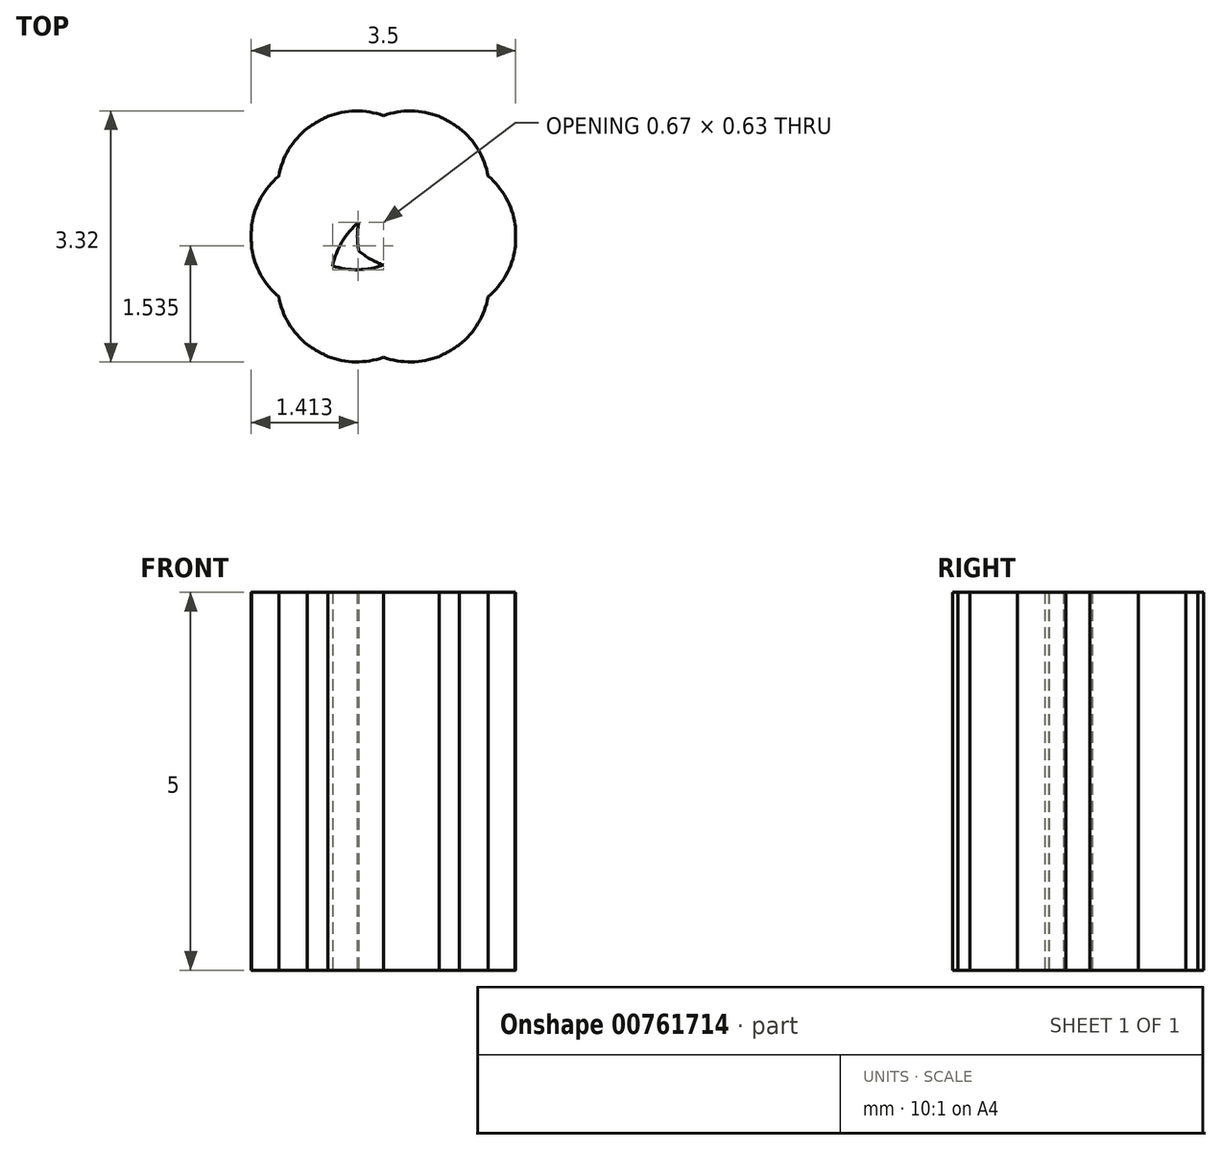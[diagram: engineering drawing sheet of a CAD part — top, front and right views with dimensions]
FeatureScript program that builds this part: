
annotation { "Feature Type Name" : "Feature", "Feature Type Description" : "" }
export const myFeature = defineFeature(function(context is Context, id is Id, definition is map)
    precondition{}
    {
        {
            var Q0;
            Q0=qCreatedBy(makeId("Top.planeOp"),FACE);
            var sketch = newSketch(context, id + "F0", { "sketchPlane" : qUnion([Q0])});
            skCircle(sketch, "E0", {"center": v(0, 0) * mm, "radius": 1.75 * mm});
            skCircle(sketch, "E1", {"center": v(-0.7, 0) * mm, "radius": 1.05 * mm});
            skCircle(sketch, "E2.1.0", {"center": v(-0.35, -0.61) * mm, "radius": 1.05 * mm});
            skCircle(sketch, "E2.2.0", {"center": v(0.35, -0.61) * mm, "radius": 1.05 * mm});
            skCircle(sketch, "E2.3.0", {"center": v(0.7, 0) * mm, "radius": 1.05 * mm});
            skCircle(sketch, "E2.4.0", {"center": v(0.35, 0.61) * mm, "radius": 1.05 * mm});
            skCircle(sketch, "E2.5.0", {"center": v(-0.35, 0.61) * mm, "radius": 1.05 * mm});
            skSolve(sketch);
        }
        {
            var Q0;
            {var subQ0=sQuery(id+"F0.wireOp",EDGE,"E2.5.0");var subQ1=sQuery(id+"F0.wireOp",EDGE,"E0");var subQ2=makeQuery(id+"F0.imprint","INTERSECT",VERTEX,{"disambiguationData":[OD(0.0)],"derivedFrom":[subQ1,subQ0]});Q0=makeQuery(id+"F0.imprint","IMPRINT",FACE,{"disambiguationData":[TD([[makeQuery(id+"F0.imprint","IMPRINT",EDGE,{"disambiguationData":[TD([[subQ2,-1.0]])],"derivedFrom":subQ1}),1.0]])]});}
            var Q1;
            {var subQ0=sQuery(id+"F0.wireOp",EDGE,"E2.4.0");var subQ1=sQuery(id+"F0.wireOp",EDGE,"E1");var subQ2=makeQuery(id+"F0.imprint","INTERSECT",VERTEX,{"disambiguationData":[OD(0.0)],"derivedFrom":[subQ1,subQ0]});Q1=makeQuery(id+"F0.imprint","IMPRINT",FACE,{"disambiguationData":[TD([[makeQuery(id+"F0.imprint","IMPRINT",EDGE,{"disambiguationData":[TD([[subQ2,-1.0]])],"derivedFrom":subQ1}),1.0]])]});}
            var Q2;
            {var subQ0=sQuery(id+"F0.wireOp",EDGE,"E2.3.0");var subQ1=sQuery(id+"F0.wireOp",EDGE,"E1");var subQ2=makeQuery(id+"F0.imprint","INTERSECT",VERTEX,{"disambiguationData":[OD(0.0)],"derivedFrom":[subQ1,subQ0]});Q2=makeQuery(id+"F0.imprint","IMPRINT",FACE,{"disambiguationData":[TD([[makeQuery(id+"F0.imprint","IMPRINT",EDGE,{"disambiguationData":[TD([[subQ2,-1.0]])],"derivedFrom":subQ1}),-1.0]])]});}
            var Q3;
            {var subQ0=sQuery(id+"F0.wireOp",EDGE,"E2.4.0");var subQ1=sQuery(id+"F0.wireOp",EDGE,"E0");var subQ2=makeQuery(id+"F0.imprint","INTERSECT",VERTEX,{"disambiguationData":[OD(0.0)],"derivedFrom":[subQ1,subQ0]});Q3=makeQuery(id+"F0.imprint","IMPRINT",FACE,{"disambiguationData":[TD([[makeQuery(id+"F0.imprint","IMPRINT",EDGE,{"disambiguationData":[TD([[subQ2,-1.0]])],"derivedFrom":subQ1}),1.0]])]});}
            var Q4;
            {var subQ0=sQuery(id+"F0.wireOp",EDGE,"E2.4.0");var subQ1=sQuery(id+"F0.wireOp",EDGE,"E2.2.0");var subQ2=makeQuery(id+"F0.imprint","INTERSECT",VERTEX,{"disambiguationData":[OD(1.0)],"derivedFrom":[subQ1,subQ0]});Q4=makeQuery(id+"F0.imprint","IMPRINT",FACE,{"disambiguationData":[TD([[makeQuery(id+"F0.imprint","IMPRINT",EDGE,{"disambiguationData":[TD([[subQ2,-1.0]])],"derivedFrom":subQ1}),-1.0]])]});}
            var Q5;
            {var subQ0=sQuery(id+"F0.wireOp",EDGE,"E2.3.0");var subQ1=sQuery(id+"F0.wireOp",EDGE,"E0");var subQ2=makeQuery(id+"F0.imprint","INTERSECT",VERTEX,{"disambiguationData":[OD(0.0)],"derivedFrom":[subQ1,subQ0]});Q5=makeQuery(id+"F0.imprint","IMPRINT",FACE,{"disambiguationData":[TD([[makeQuery(id+"F0.imprint","IMPRINT",EDGE,{"disambiguationData":[TD([[subQ2,1.0]])],"derivedFrom":subQ1}),1.0]])]});}
            var Q6;
            {var subQ0=sQuery(id+"F0.wireOp",EDGE,"E2.3.0");var subQ1=sQuery(id+"F0.wireOp",EDGE,"E2.1.0");var subQ2=makeQuery(id+"F0.imprint","INTERSECT",VERTEX,{"disambiguationData":[OD(1.0)],"derivedFrom":[subQ1,subQ0]});Q6=makeQuery(id+"F0.imprint","IMPRINT",FACE,{"disambiguationData":[TD([[makeQuery(id+"F0.imprint","IMPRINT",EDGE,{"disambiguationData":[TD([[subQ2,-1.0]])],"derivedFrom":subQ1}),-1.0]])]});}
            var Q7;
            {var subQ0=sQuery(id+"F0.wireOp",EDGE,"E2.2.0");var subQ1=sQuery(id+"F0.wireOp",EDGE,"E0");var subQ8=makeQuery(id+"F0.imprint","INTERSECT",VERTEX,{"disambiguationData":[OD(0.0)],"derivedFrom":[subQ1,subQ0]});Q7=makeQuery(id+"F0.imprint","IMPRINT",FACE,{"disambiguationData":[TD([[makeQuery(id+"F0.imprint","IMPRINT",EDGE,{"disambiguationData":[TD([[subQ8,-1.0]])],"derivedFrom":subQ1}),1.0]])]});}
            var Q8;
            {var subQ0=sQuery(id+"F0.wireOp",EDGE,"E2.2.0");var subQ1=sQuery(id+"F0.wireOp",EDGE,"E1");var subQ2=makeQuery(id+"F0.imprint","INTERSECT",VERTEX,{"disambiguationData":[OD(1.0)],"derivedFrom":[subQ1,subQ0]});Q8=makeQuery(id+"F0.imprint","IMPRINT",FACE,{"disambiguationData":[TD([[makeQuery(id+"F0.imprint","IMPRINT",EDGE,{"disambiguationData":[TD([[subQ2,-1.0]])],"derivedFrom":subQ1}),-1.0]])]});}
            var Q9;
            {var subQ0=sQuery(id+"F0.wireOp",EDGE,"E2.1.0");var subQ1=sQuery(id+"F0.wireOp",EDGE,"E0");var subQ8=makeQuery(id+"F0.imprint","INTERSECT",VERTEX,{"disambiguationData":[OD(0.0)],"derivedFrom":[subQ1,subQ0]});Q9=makeQuery(id+"F0.imprint","IMPRINT",FACE,{"disambiguationData":[TD([[makeQuery(id+"F0.imprint","IMPRINT",EDGE,{"disambiguationData":[TD([[subQ8,-1.0]])],"derivedFrom":subQ1}),1.0]])]});}
            var Q10;
            {var subQ1=sQuery(id+"F0.wireOp",EDGE,"E1");var subQ5=sQuery(id+"F0.wireOp",EDGE,"E0");var subQ6=makeQuery(id+"F0.imprint","INTERSECT",VERTEX,{"disambiguationData":[OD(0.0)],"derivedFrom":[subQ5,subQ1]});Q10=makeQuery(id+"F0.imprint","IMPRINT",FACE,{"disambiguationData":[TD([[makeQuery(id+"F0.imprint","IMPRINT",EDGE,{"disambiguationData":[TD([[subQ6,-1.0]])],"derivedFrom":subQ5}),1.0]])]});}
            var Q11;
            {var subQ0=sQuery(id+"F0.wireOp",EDGE,"E2.1.0");var subQ1=sQuery(id+"F0.wireOp",EDGE,"E1");var subQ2=makeQuery(id+"F0.imprint","INTERSECT",VERTEX,{"disambiguationData":[OD(1.0)],"derivedFrom":[subQ1,subQ0]});Q11=makeQuery(id+"F0.imprint","IMPRINT",FACE,{"disambiguationData":[TD([[makeQuery(id+"F0.imprint","IMPRINT",EDGE,{"disambiguationData":[TD([[subQ2,-1.0]])],"derivedFrom":subQ1}),1.0]])]});}
            var Q12;
            {var subQ0=sQuery(id+"F0.wireOp",EDGE,"E2.2.0");var subQ1=sQuery(id+"F0.wireOp",EDGE,"E1");var subQ2=makeQuery(id+"F0.imprint","INTERSECT",VERTEX,{"disambiguationData":[OD(1.0)],"derivedFrom":[subQ1,subQ0]});Q12=makeQuery(id+"F0.imprint","IMPRINT",FACE,{"disambiguationData":[TD([[makeQuery(id+"F0.imprint","IMPRINT",EDGE,{"disambiguationData":[TD([[subQ2,-1.0]])],"derivedFrom":subQ1}),1.0]])]});}
            var Q13;
            {var subQ0=sQuery(id+"F0.wireOp",EDGE,"E2.3.0");var subQ1=sQuery(id+"F0.wireOp",EDGE,"E1");var subQ2=makeQuery(id+"F0.imprint","INTERSECT",VERTEX,{"disambiguationData":[OD(1.0)],"derivedFrom":[subQ1,subQ0]});Q13=makeQuery(id+"F0.imprint","IMPRINT",FACE,{"disambiguationData":[TD([[makeQuery(id+"F0.imprint","IMPRINT",EDGE,{"disambiguationData":[TD([[subQ2,-1.0]])],"derivedFrom":subQ1}),-1.0]])]});}
            var Q14;
            {var subQ0=sQuery(id+"F0.wireOp",EDGE,"E2.3.0");var subQ1=sQuery(id+"F0.wireOp",EDGE,"E1");var subQ2=makeQuery(id+"F0.imprint","INTERSECT",VERTEX,{"disambiguationData":[OD(1.0)],"derivedFrom":[subQ1,subQ0]});Q14=makeQuery(id+"F0.imprint","IMPRINT",FACE,{"disambiguationData":[TD([[makeQuery(id+"F0.imprint","IMPRINT",EDGE,{"disambiguationData":[TD([[subQ2,-1.0]])],"derivedFrom":subQ1}),1.0]])]});}
            var Q15;
            {var subQ0=sQuery(id+"F0.wireOp",EDGE,"E2.4.0");var subQ1=sQuery(id+"F0.wireOp",EDGE,"E2.1.0");var subQ2=makeQuery(id+"F0.imprint","INTERSECT",VERTEX,{"disambiguationData":[OD(1.0)],"derivedFrom":[subQ1,subQ0]});Q15=makeQuery(id+"F0.imprint","IMPRINT",FACE,{"disambiguationData":[TD([[makeQuery(id+"F0.imprint","IMPRINT",EDGE,{"disambiguationData":[TD([[subQ2,-1.0]])],"derivedFrom":subQ1}),-1.0]])]});}
            var Q16;
            {var subQ0=sQuery(id+"F0.wireOp",EDGE,"E2.2.0");var subQ1=sQuery(id+"F0.wireOp",EDGE,"E1");var subQ2=makeQuery(id+"F0.imprint","INTERSECT",VERTEX,{"disambiguationData":[OD(0.0)],"derivedFrom":[subQ1,subQ0]});Q16=makeQuery(id+"F0.imprint","IMPRINT",FACE,{"disambiguationData":[TD([[makeQuery(id+"F0.imprint","IMPRINT",EDGE,{"disambiguationData":[TD([[subQ2,-1.0]])],"derivedFrom":subQ1}),-1.0]])]});}
            var Q17;
            {var subQ0=sQuery(id+"F0.wireOp",EDGE,"E2.3.0");var subQ1=sQuery(id+"F0.wireOp",EDGE,"E1");var subQ2=makeQuery(id+"F0.imprint","INTERSECT",VERTEX,{"disambiguationData":[OD(0.0)],"derivedFrom":[subQ1,subQ0]});Q17=makeQuery(id+"F0.imprint","IMPRINT",FACE,{"disambiguationData":[TD([[makeQuery(id+"F0.imprint","IMPRINT",EDGE,{"disambiguationData":[TD([[subQ2,-1.0]])],"derivedFrom":subQ1}),1.0]])]});}
            var Q18;
            {var subQ0=sQuery(id+"F0.wireOp",EDGE,"E2.4.0");var subQ1=sQuery(id+"F0.wireOp",EDGE,"E2.1.0");var subQ2=makeQuery(id+"F0.imprint","INTERSECT",VERTEX,{"disambiguationData":[OD(0.0)],"derivedFrom":[subQ1,subQ0]});Q18=makeQuery(id+"F0.imprint","IMPRINT",FACE,{"disambiguationData":[TD([[makeQuery(id+"F0.imprint","IMPRINT",EDGE,{"disambiguationData":[TD([[subQ2,-1.0]])],"derivedFrom":subQ1}),1.0]])]});}
            var Q19;
            {var subQ0=sQuery(id+"F0.wireOp",EDGE,"E2.2.0");var subQ1=sQuery(id+"F0.wireOp",EDGE,"E1");var subQ2=makeQuery(id+"F0.imprint","INTERSECT",VERTEX,{"disambiguationData":[OD(0.0)],"derivedFrom":[subQ1,subQ0]});Q19=makeQuery(id+"F0.imprint","IMPRINT",FACE,{"disambiguationData":[TD([[makeQuery(id+"F0.imprint","IMPRINT",EDGE,{"disambiguationData":[TD([[subQ2,-1.0]])],"derivedFrom":subQ1}),1.0]])]});}
            var Q20;
            {var subQ0=sQuery(id+"F0.wireOp",EDGE,"E2.4.0");var subQ1=sQuery(id+"F0.wireOp",EDGE,"E1");var subQ2=makeQuery(id+"F0.imprint","INTERSECT",VERTEX,{"disambiguationData":[OD(1.0)],"derivedFrom":[subQ1,subQ0]});Q20=makeQuery(id+"F0.imprint","IMPRINT",FACE,{"disambiguationData":[TD([[makeQuery(id+"F0.imprint","IMPRINT",EDGE,{"disambiguationData":[TD([[subQ2,-1.0]])],"derivedFrom":subQ1}),-1.0]])]});}
            var Q21;
            {var subQ0=sQuery(id+"F0.wireOp",EDGE,"E2.4.0");var subQ1=sQuery(id+"F0.wireOp",EDGE,"E2.2.0");var subQ2=makeQuery(id+"F0.imprint","INTERSECT",VERTEX,{"disambiguationData":[OD(0.0)],"derivedFrom":[subQ1,subQ0]});Q21=makeQuery(id+"F0.imprint","IMPRINT",FACE,{"disambiguationData":[TD([[makeQuery(id+"F0.imprint","IMPRINT",EDGE,{"disambiguationData":[TD([[subQ2,-1.0]])],"derivedFrom":subQ1}),1.0]])]});}
            var Q22;
            {var subQ0=sQuery(id+"F0.wireOp",EDGE,"E2.3.0");var subQ1=sQuery(id+"F0.wireOp",EDGE,"E2.1.0");var subQ2=makeQuery(id+"F0.imprint","INTERSECT",VERTEX,{"disambiguationData":[OD(0.0)],"derivedFrom":[subQ1,subQ0]});Q22=makeQuery(id+"F0.imprint","IMPRINT",FACE,{"disambiguationData":[TD([[makeQuery(id+"F0.imprint","IMPRINT",EDGE,{"disambiguationData":[TD([[subQ2,-1.0]])],"derivedFrom":subQ1}),1.0]])]});}
            var Q23;
            {var subQ0=sQuery(id+"F0.wireOp",EDGE,"E2.2.0");var subQ1=sQuery(id+"F0.wireOp",EDGE,"E1");var subQ2=makeQuery(id+"F0.imprint","INTERSECT",VERTEX,{"disambiguationData":[OD(0.0)],"derivedFrom":[subQ1,subQ0]});Q23=makeQuery(id+"F0.imprint","IMPRINT",FACE,{"disambiguationData":[TD([[makeQuery(id+"F0.imprint","IMPRINT",EDGE,{"disambiguationData":[TD([[subQ2,1.0]])],"derivedFrom":subQ1}),-1.0]])]});}
            var Q24;
            {var subQ0=sQuery(id+"F0.wireOp",EDGE,"E2.4.0");var subQ1=sQuery(id+"F0.wireOp",EDGE,"E2.2.0");var subQ2=makeQuery(id+"F0.imprint","INTERSECT",VERTEX,{"disambiguationData":[OD(0.0)],"derivedFrom":[subQ1,subQ0]});Q24=makeQuery(id+"F0.imprint","IMPRINT",FACE,{"disambiguationData":[TD([[makeQuery(id+"F0.imprint","IMPRINT",EDGE,{"disambiguationData":[TD([[subQ2,1.0]])],"derivedFrom":subQ1}),1.0]])]});}
            var Q25;
            {var subQ0=sQuery(id+"F0.wireOp",EDGE,"E2.5.0");var subQ1=sQuery(id+"F0.wireOp",EDGE,"E2.3.0");var subQ2=makeQuery(id+"F0.imprint","INTERSECT",VERTEX,{"disambiguationData":[OD(0.0)],"derivedFrom":[subQ1,subQ0]});Q25=makeQuery(id+"F0.imprint","IMPRINT",FACE,{"disambiguationData":[TD([[makeQuery(id+"F0.imprint","IMPRINT",EDGE,{"disambiguationData":[TD([[subQ2,1.0]])],"derivedFrom":subQ1}),1.0]])]});}
            var Q26;
            {var subQ0=sQuery(id+"F0.wireOp",EDGE,"E2.4.0");var subQ1=sQuery(id+"F0.wireOp",EDGE,"E1");var subQ2=makeQuery(id+"F0.imprint","INTERSECT",VERTEX,{"disambiguationData":[OD(1.0)],"derivedFrom":[subQ1,subQ0]});Q26=makeQuery(id+"F0.imprint","IMPRINT",FACE,{"disambiguationData":[TD([[makeQuery(id+"F0.imprint","IMPRINT",EDGE,{"disambiguationData":[TD([[subQ2,-1.0]])],"derivedFrom":subQ1}),1.0]])]});}
            var Q27;
            {var subQ0=sQuery(id+"F0.wireOp",EDGE,"E2.1.0");var subQ1=sQuery(id+"F0.wireOp",EDGE,"E1");var subQ2=makeQuery(id+"F0.imprint","INTERSECT",VERTEX,{"disambiguationData":[OD(0.0)],"derivedFrom":[subQ1,subQ0]});Q27=makeQuery(id+"F0.imprint","IMPRINT",FACE,{"disambiguationData":[TD([[makeQuery(id+"F0.imprint","IMPRINT",EDGE,{"disambiguationData":[TD([[subQ2,1.0]])],"derivedFrom":subQ1}),-1.0]])]});}
            var Q28;
            {var subQ5=sQuery(id+"F0.wireOp",EDGE,"E2.1.0");var subQ7=sQuery(id+"F0.wireOp",EDGE,"E1");var subQ8=makeQuery(id+"F0.imprint","INTERSECT",VERTEX,{"disambiguationData":[OD(0.0)],"derivedFrom":[subQ7,subQ5]});Q28=makeQuery(id+"F0.imprint","IMPRINT",FACE,{"disambiguationData":[TD([[makeQuery(id+"F0.imprint","IMPRINT",EDGE,{"disambiguationData":[TD([[subQ8,1.0]])],"derivedFrom":subQ7}),1.0]])]});}
            var Q29;
            {var subQ0=sQuery(id+"F0.wireOp",EDGE,"E2.2.0");var subQ1=sQuery(id+"F0.wireOp",EDGE,"E1");var subQ2=makeQuery(id+"F0.imprint","INTERSECT",VERTEX,{"disambiguationData":[OD(0.0)],"derivedFrom":[subQ1,subQ0]});Q29=makeQuery(id+"F0.imprint","IMPRINT",FACE,{"disambiguationData":[TD([[makeQuery(id+"F0.imprint","IMPRINT",EDGE,{"disambiguationData":[TD([[subQ2,1.0]])],"derivedFrom":subQ1}),1.0]])]});}
            var Q30;
            {var subQ0=sQuery(id+"F0.wireOp",EDGE,"E2.3.0");var subQ1=sQuery(id+"F0.wireOp",EDGE,"E2.1.0");var subQ2=makeQuery(id+"F0.imprint","INTERSECT",VERTEX,{"disambiguationData":[OD(0.0)],"derivedFrom":[subQ1,subQ0]});Q30=makeQuery(id+"F0.imprint","IMPRINT",FACE,{"disambiguationData":[TD([[makeQuery(id+"F0.imprint","IMPRINT",EDGE,{"disambiguationData":[TD([[subQ2,1.0]])],"derivedFrom":subQ1}),1.0]])]});}
            extrude(context, id + "F1", {"entities" : qUnion([Q0, Q1, Q2, Q3, Q4, Q5, Q6, Q7, Q8, Q9, Q10, Q11, Q12, Q13, Q14, Q15, Q16, Q17, Q18, Q19, Q20, Q21, Q22, Q23, Q24, Q25, Q26, Q27, Q28, Q29, Q30]), "depth" : 5 * mm, "offsetDistance" : 25 * mm});
        }
    });
